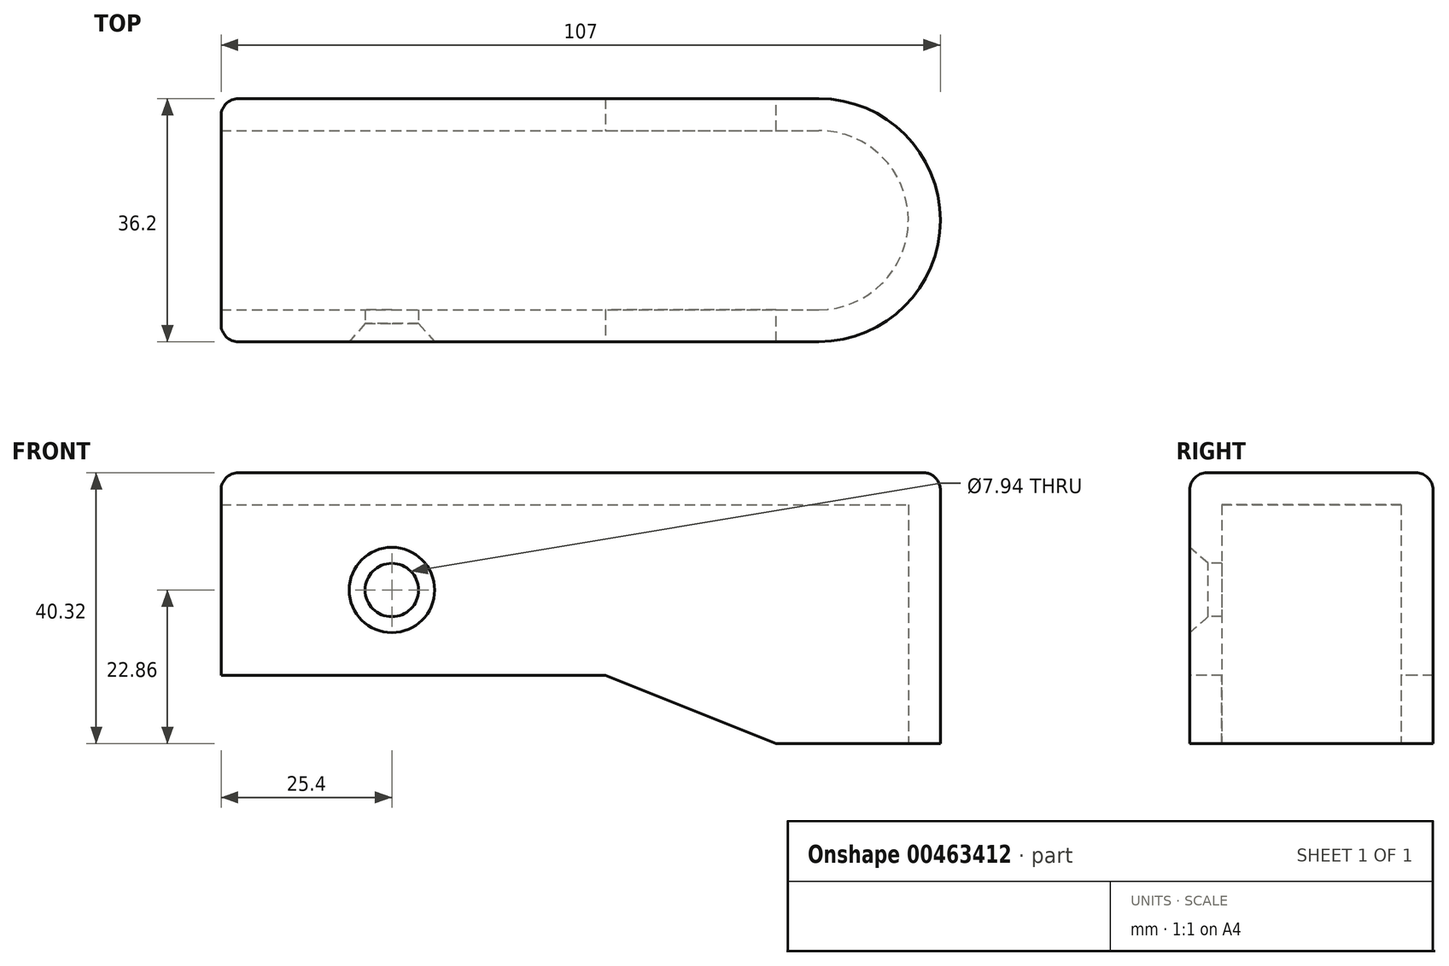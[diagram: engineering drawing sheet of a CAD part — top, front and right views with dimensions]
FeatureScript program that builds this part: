
annotation { "Feature Type Name" : "Feature", "Feature Type Description" : "" }
export const myFeature = defineFeature(function(context is Context, id is Id, definition is map)
    precondition{}
    {
        {
            var Q0;
            Q0=qCreatedBy(makeId("Top.planeOp"),FACE);
            var sketch = newSketch(context, id + "F0", { "sketchPlane" : qUnion([Q0])});
            skLineSegment(sketch, "E0.bottom", {"start": v(-50.8, 18.1) * mm, "end": v(38.1, 18.1) * mm});
            skLineSegment(sketch, "E0.top", {"start": v(-50.8, -18.1) * mm, "end": v(38.1, -18.1) * mm});
            skLineSegment(sketch, "E0.left", {"start": v(-50.8, 18.1) * mm, "end": v(-50.8, 13.33) * mm});
            skLineSegment(sketch, "E1.bottom", {"start": v(-50.8, 13.33) * mm, "end": v(38.1, 13.33) * mm});
            skLineSegment(sketch, "E1.top", {"start": v(-50.8, -13.34) * mm, "end": v(38.1, -13.34) * mm});
            skLineSegment(sketch, "E2.trimOffspring", {"start": v(-50.8, -13.34) * mm, "end": v(-50.8, -18.1) * mm});
            skArc(sketch, "E3", {"start": v(38.1, -18.1) * mm, "mid": v(56.2, 0) * mm, "end": v(38.1, 18.1) * mm});
            skArc(sketch, "E4", {"start": v(38.1, -13.34) * mm, "mid": v(51.44, 0) * mm, "end": v(38.1, 13.34) * mm});
            skSolve(sketch);
        }
        {
            var Q0;
            Q0=makeQuery(id+"F0.imprint","IMPRINT",FACE,{"disambiguationData":[TD([[makeQuery(id+"F0.imprint","IMPRINT",EDGE,{"derivedFrom":sQuery(id+"F0.wireOp",EDGE,"E0.bottom")}),-1.0]])]});
            extrude(context, id + "F1", {"entities" : qUnion([Q0]), "depth" : 25.4 * mm});
        }
        {
            var Q0;
            Q0=makeQuery(id+"F1.opExtrude","CAP_FACE",FACE,{"disambiguationData":[OSD([sQuery(id+"F0.wireOp",EDGE,"E0.bottom"),sQuery(id+"F0.wireOp",EDGE,"E0.top"),sQuery(id+"F0.wireOp",EDGE,"E0.left"),sQuery(id+"F0.wireOp",EDGE,"E0.right"),sQuery(id+"F0.wireOp",EDGE,"E1.bottom"),sQuery(id+"F0.wireOp",EDGE,"E1.top"),sQuery(id+"F0.wireOp",EDGE,"E1.right"),sQuery(id+"F0.wireOp",EDGE,"E2.trimOffspring")])],"isStart":false});
            var sketch = newSketch(context, id + "F2", { "sketchPlane" : qUnion([Q0])});
            skLineSegment(sketch, "E5.bottom", {"start": v(-50.8, 18.1) * mm, "end": v(-50.8, 18.1) * mm});
            skLineSegment(sketch, "E5.top", {"start": v(-50.8, -18.1) * mm, "end": v(-50.8, -18.1) * mm});
            skLineSegment(sketch, "E5.left", {"start": v(-50.8, 18.1) * mm, "end": v(-50.8, -18.1) * mm});
            skLineSegment(sketch, "E5.right", {"start": v(-50.8, 18.1) * mm, "end": v(-50.8, -18.1) * mm});
            skLineSegment(sketch, "E6", {"start": v(-50.8, 18.1) * mm, "end": v(38.1, 18.1) * mm});
            skLineSegment(sketch, "E7", {"start": v(-50.8, -18.1) * mm, "end": v(38.1, -18.1) * mm});
            skPoint(sketch, "E8.center.orphan", {"position": v(38.1, 0) * mm});
            skArc(sketch, "E9", {"start": v(38.1, -18.1) * mm, "mid": v(56.2, 0) * mm, "end": v(38.1, 18.1) * mm});
            skSolve(sketch);
        }
        {
            var Q0;
            {var subQ1=makeQuery(id+"F1.opExtrude","CAP_EDGE",EDGE,{"disambiguationData":[OSD([sQuery(id+"F0.wireOp",EDGE,"E1.bottom")])],"isStart":false});Q0=makeQuery(id+"F2.imprint","IMPRINT",FACE,{"disambiguationData":[TD([[makeQuery(id+"F2.imprint","IMPRINT",EDGE,{"derivedFrom":subQ1}),-1.0]])]});}
            var Q1;
            {var subQ1=sQuery(id+"F2.wireOp",EDGE,"E5.bottom");Q1=makeQuery(id+"F2.imprint","IMPRINT",FACE,{"disambiguationData":[TD([[makeQuery(id+"F2.imprint","IMPRINT",EDGE,{"derivedFrom":subQ1}),-1.0]])]});}
            var Q2;
            {var subQ1=sQuery(id+"F2.wireOp",EDGE,"E6");Q2=makeQuery(id+"F2.imprint","IMPRINT",FACE,{"disambiguationData":[TD([[makeQuery(id+"F2.imprint","IMPRINT",EDGE,{"derivedFrom":subQ1}),-1.0]])]});}
            extrude(context, id + "F3", {"entities" : qUnion([Q0, Q1, Q2]), "operationType" : NewBodyOperationType.ADD, "depth" : 4.76 * mm});
        }
        {
            var Q0;
            Q0=makeQuery(id+"F3.boolean.opBoolean","MERGE",FACE,{"derivedFrom":[makeQuery(id+"F1.opExtrude","SWEPT_FACE",FACE,{"disambiguationData":[OSD([sQuery(id+"F0.wireOp",EDGE,"E0.top")])]}),makeQuery(id+"F3.opExtrude","SWEPT_FACE",FACE,{"disambiguationData":[OSD([sQuery(id+"F2.wireOp",EDGE,"E5.top")])]})]});
            var sketch = newSketch(context, id + "F4", { "sketchPlane" : qUnion([Q0])});
            skPoint(sketch, "E10", {"position": v(-25.4, 12.7) * mm});
            skSolve(sketch);
        }
        {
            var Q0;
            Q0=sQuery(id+"F4.wireOp",VERTEX,"E10");
            var Q1;
            Q1=makeQuery(id+"F1.opExtrude","SWEPT_BODY",BODY,{"disambiguationData":[OSD([sQuery(id+"F0.wireOp",EDGE,"E0.bottom"),sQuery(id+"F0.wireOp",EDGE,"E0.top"),sQuery(id+"F0.wireOp",EDGE,"E0.left"),sQuery(id+"F0.wireOp",EDGE,"E0.right"),sQuery(id+"F0.wireOp",EDGE,"E1.bottom"),sQuery(id+"F0.wireOp",EDGE,"E1.top"),sQuery(id+"F0.wireOp",EDGE,"E1.right"),sQuery(id+"F0.wireOp",EDGE,"E2.trimOffspring")])]});
            hole(context, id + "F5", {"style" : HoleStyle.C_SINK, "endStyle" : HoleEndStyle.BLIND, "holeDiameter" : 7.94 * mm, "cSinkDiameter" : 12.7 * mm, "cSinkAngle" : 82 * degree, "holeDepth" : 12.7 * mm, "isTappedThrough" : true, "tappedDepth" : 12.7 * mm, "tapClearance" : 3, "locations" : qUnion([Q0]), "scope" : qUnion([Q1])});
        }
        {
            var Q0;
            Q0=makeQuery(id+"F3.opExtrude","CAP_EDGE",EDGE,{"disambiguationData":[OSD([sQuery(id+"F2.wireOp",EDGE,"E5.top")])],"isStart":false});
            var Q1;
            Q1=makeQuery(id+"F3.boolean.opBoolean","MERGE",EDGE,{"derivedFrom":[makeQuery(id+"F1.opExtrude","SWEPT_EDGE",EDGE,{"disambiguationData":[OSD([sQuery(id+"F0.wireOp",EDGE,"E0.top"),sQuery(id+"F0.wireOp",EDGE,"E0.right")])]}),makeQuery(id+"F3.opExtrude","SWEPT_EDGE",EDGE,{"disambiguationData":[OSD([sQuery(id+"F2.wireOp",EDGE,"E5.top"),sQuery(id+"F2.wireOp",EDGE,"E5.left")])]})]});
            var Q2;
            Q2=makeQuery(id+"F3.opExtrude","CAP_EDGE",EDGE,{"disambiguationData":[OSD([sQuery(id+"F2.wireOp",EDGE,"E5.left")])],"isStart":false});
            var Q3;
            Q3=makeQuery(id+"F3.boolean.opBoolean","MERGE",EDGE,{"derivedFrom":[makeQuery(id+"F1.opExtrude","SWEPT_EDGE",EDGE,{"disambiguationData":[OSD([sQuery(id+"F0.wireOp",EDGE,"E0.bottom"),sQuery(id+"F0.wireOp",EDGE,"E0.right")])]}),makeQuery(id+"F3.opExtrude","SWEPT_EDGE",EDGE,{"disambiguationData":[OSD([sQuery(id+"F2.wireOp",EDGE,"E5.bottom"),sQuery(id+"F2.wireOp",EDGE,"E5.left")])]})]});
            var Q4;
            Q4=makeQuery(id+"F3.opExtrude","CAP_EDGE",EDGE,{"disambiguationData":[OSD([sQuery(id+"F2.wireOp",EDGE,"E5.bottom")])],"isStart":false});
            var Q5;
            Q5=makeQuery(id+"F3.opExtrude","CAP_EDGE",EDGE,{"disambiguationData":[OSD([sQuery(id+"F2.wireOp",EDGE,"E6")])],"isStart":false});
            var Q6;
            Q6=makeQuery(id+"F3.opExtrude","CAP_EDGE",EDGE,{"disambiguationData":[OSD([sQuery(id+"F2.wireOp",EDGE,"E5.right")])],"isStart":false});
            fillet(context, id + "F6", {"entities" : qUnion([Q0, Q1, Q2, Q3, Q4, Q5, Q6]), "radius" : 2.54 * mm, "tangentPropagation" : true, "allowEdgeOverflow" : false});
        }
        {
            var Q0;
            Q0=makeQuery(id+"F1.opExtrude","CAP_FACE",FACE,{"disambiguationData":[OSD([sQuery(id+"F0.wireOp",EDGE,"E0.bottom"),sQuery(id+"F0.wireOp",EDGE,"E0.top"),sQuery(id+"F0.wireOp",EDGE,"E0.left"),sQuery(id+"F0.wireOp",EDGE,"E1.bottom"),sQuery(id+"F0.wireOp",EDGE,"E1.top"),sQuery(id+"F0.wireOp",EDGE,"E2.trimOffspring"),sQuery(id+"F0.wireOp",EDGE,"E3"),sQuery(id+"F0.wireOp",EDGE,"E4")])],"isStart":true});
            var sketch = newSketch(context, id + "F7", { "sketchPlane" : qUnion([Q0])});
            skLineSegment(sketch, "E11", {"start": v(38.1, 18.1) * mm, "end": v(0, 18.1) * mm});
            skLineSegment(sketch, "E12", {"start": v(0, 18.1) * mm, "end": v(0, 13.34) * mm});
            skLineSegment(sketch, "E13", {"start": v(0, -13.33) * mm, "end": v(0, -18.1) * mm});
            skLineSegment(sketch, "E14", {"start": v(0, -18.1) * mm, "end": v(38.1, -18.1) * mm});
            skLineSegment(sketch, "E15", {"start": v(0, 13.34) * mm, "end": v(38.1, 13.33) * mm});
            skLineSegment(sketch, "E16", {"start": v(0, -13.33) * mm, "end": v(38.1, -13.33) * mm});
            skPoint(sketch, "E17.center.orphan", {"position": v(38.1, 0) * mm});
            skArc(sketch, "E18", {"start": v(38.1, 18.1) * mm, "mid": v(56.2, 0) * mm, "end": v(38.1, -18.1) * mm});
            skArc(sketch, "E19", {"start": v(38.1, 13.33) * mm, "mid": v(51.44, 0) * mm, "end": v(38.1, -13.33) * mm});
            skSolve(sketch);
        }
        {
            var Q0;
            Q0 = qSketchRegion(id + "F7", true);
            extrude(context, id + "F8", {"entities" : qUnion([Q0]), "operationType" : NewBodyOperationType.ADD, "depth" : 10.16 * mm});
        }
        {
            var Q0;
            Q0=makeQuery(id+"F8.opExtrude","CAP_EDGE",EDGE,{"disambiguationData":[OSD([sQuery(id+"F7.wireOp",EDGE,"E13")])],"isStart":false});
            var Q1;
            Q1=makeQuery(id+"F8.opExtrude","CAP_EDGE",EDGE,{"disambiguationData":[OSD([sQuery(id+"F7.wireOp",EDGE,"E12")])],"isStart":false});
            chamfer(context, id + "F9", {"entities" : qUnion([Q0, Q1]), "chamferType" : ChamferType.TWO_OFFSETS, "width1" : 31.75 * mm, "oppositeDirection" : false, "width2" : 12.7 * mm, "tangentPropagation" : true});
        }
    });
